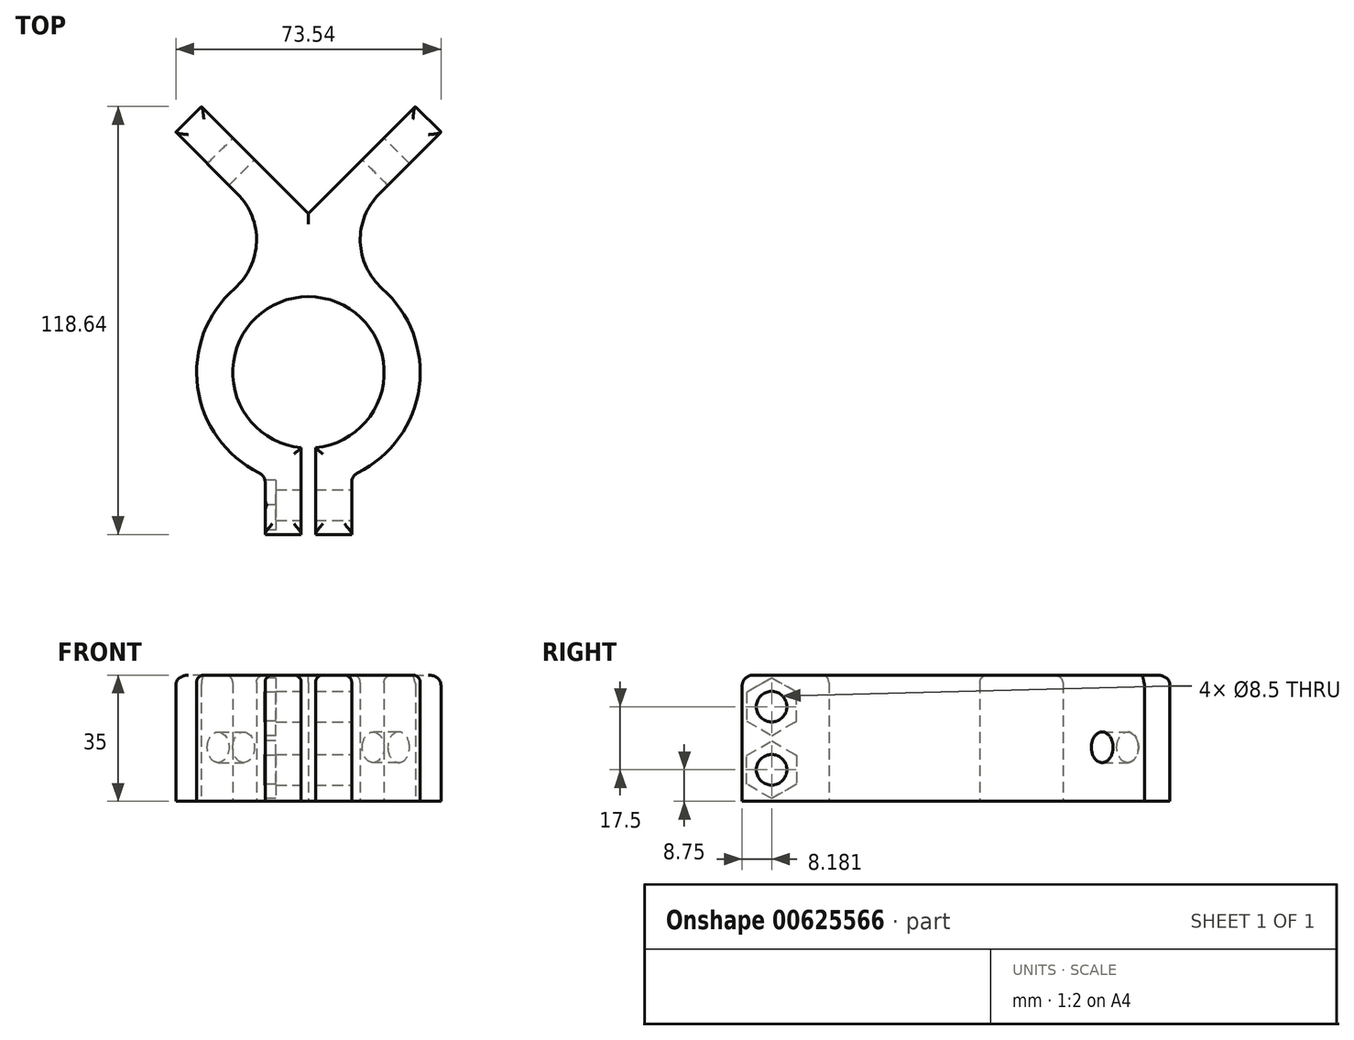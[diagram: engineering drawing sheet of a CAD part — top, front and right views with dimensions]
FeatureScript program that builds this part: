
annotation { "Feature Type Name" : "Feature", "Feature Type Description" : "" }
export const myFeature = defineFeature(function(context is Context, id is Id, definition is map)
    precondition{}
    {
        {
            var Q0;
            Q0=qCreatedBy(makeId("Top.planeOp"),FACE);
            var sketch = newSketch(context, id + "F0", { "sketchPlane" : qUnion([Q0])});
            skLineSegment(sketch, "E0", {"start": v(0, 0) * mm, "end": v(-29.7, 29.7) * mm});
            skLineSegment(sketch, "E1", {"start": v(0, 38.94) * mm, "end": v(0, 0) * mm, "construction": true});
            skLineSegment(sketch, "E2", {"start": v(-29.7, 29.7) * mm, "end": v(-36.77, 22.63) * mm});
            skLineSegment(sketch, "E3", {"start": v(-36.77, 22.63) * mm, "end": v(-1.12, -13.02) * mm});
            skLineSegment(sketch, "E4", {"start": v(0, 0) * mm, "end": v(0, -44) * mm, "construction": true});
            skArc(sketch, "E5", {"start": v(2, -64.9) * mm, "mid": v(0, -23) * mm, "end": v(-2, -64.9) * mm});
            skArc(sketch, "E6", {"start": v(2, -74.94) * mm, "mid": v(31, -43.56) * mm, "end": v(1.12, -13.02) * mm});
            skLineSegment(sketch, "E7", {"start": v(0, -44) * mm, "end": v(0, -75) * mm, "construction": true});
            skLineSegment(sketch, "E8", {"start": v(-2, -74.94) * mm, "end": v(-2, -88.94) * mm});
            skLineSegment(sketch, "E9", {"start": v(-2, -88.94) * mm, "end": v(-12, -88.94) * mm});
            skLineSegment(sketch, "E10", {"start": v(-12, -88.94) * mm, "end": v(-12, -72.58) * mm});
            skLineSegment(sketch, "E11.MirrorCS", {"start": v(2, -88.94) * mm, "end": v(12, -88.94) * mm});
            skLineSegment(sketch, "E12.MirrorCS", {"start": v(12, -88.94) * mm, "end": v(12, -72.58) * mm});
            skLineSegment(sketch, "E13.MirrorCS", {"start": v(2, -74.94) * mm, "end": v(2, -88.94) * mm});
            skLineSegment(sketch, "E14", {"start": v(-2, -74.94) * mm, "end": v(-2, -64.9) * mm});
            skLineSegment(sketch, "E15.MirrorCS", {"start": v(2, -74.94) * mm, "end": v(2, -64.9) * mm});
            skLineSegment(sketch, "E16.MirrorCS", {"start": v(29.7, 29.7) * mm, "end": v(36.77, 22.63) * mm});
            skLineSegment(sketch, "E17.MirrorCS", {"start": v(0, 0) * mm, "end": v(29.7, 29.7) * mm});
            skLineSegment(sketch, "E18.MirrorCS", {"start": v(36.77, 22.63) * mm, "end": v(1.12, -13.02) * mm});
            skPoint(sketch, "E19.orphan", {"position": v(0, -14.14) * mm});
            skArc(sketch, "E20.trimOffspring", {"start": v(-1.12, -13.02) * mm, "mid": v(-31, -43.56) * mm, "end": v(-2, -74.94) * mm});
            skSolve(sketch);
        }
        {
            var Q0;
            Q0=makeQuery(id+"F0.imprint","IMPRINT",FACE,{"disambiguationData":[TD([[makeQuery(id+"F0.imprint","IMPRINT",EDGE,{"derivedFrom":sQuery(id+"F0.wireOp",EDGE,"E0")}),1.0]])]});
            var Q1;
            {var subQ4=sQuery(id+"F0.wireOp",EDGE,"E9");Q1=makeQuery(id+"F0.imprint","IMPRINT",FACE,{"disambiguationData":[TD([[makeQuery(id+"F0.imprint","IMPRINT",EDGE,{"derivedFrom":subQ4}),-1.0]])]});}
            var Q2;
            {var subQ1=sQuery(id+"F0.wireOp",EDGE,"E11.MirrorCS");Q2=makeQuery(id+"F0.imprint","IMPRINT",FACE,{"disambiguationData":[TD([[makeQuery(id+"F0.imprint","IMPRINT",EDGE,{"derivedFrom":subQ1}),1.0]])]});}
            extrude(context, id + "F1", {"entities" : qUnion([Q0, Q1, Q2]), "depth" : 35 * mm, "offsetDistance" : 25 * mm});
        }
        {
            var Q0;
            Q0=makeQuery(id+"F1.opExtrude","SWEPT_FACE",FACE,{"disambiguationData":[OSD([sQuery(id+"F0.wireOp",EDGE,"E17.MirrorCS")])]});
            var sketch = newSketch(context, id + "F2", { "sketchPlane" : qUnion([Q0])});
            skLineSegment(sketch, "E21", {"start": v(0, 15) * mm, "end": v(-50.8, 15) * mm, "construction": true});
            skCircle(sketch, "E22", {"center": v(-25.4, 15) * mm, "radius": 4.25 * mm});
            skSolve(sketch);
        }
        {
            var Q0;
            Q0 = qSketchRegion(id + "F2", true);
            extrude(context, id + "F3", {"entities" : qUnion([Q0]), "operationType" : NewBodyOperationType.REMOVE, "endBound" : BoundingType.UP_TO_NEXT, "oppositeDirection" : true, "depth" : 25 * mm, "offsetDistance" : 25 * mm});
        }
        {
            var Q0;
            Q0=makeQuery(id+"F1.opExtrude","SWEPT_FACE",FACE,{"disambiguationData":[OSD([sQuery(id+"F0.wireOp",EDGE,"E0")])]});
            var sketch = newSketch(context, id + "F4", { "sketchPlane" : qUnion([Q0])});
            skLineSegment(sketch, "E23", {"start": v(0, 15) * mm, "end": v(50.8, 15) * mm, "construction": true});
            skCircle(sketch, "E24", {"center": v(25.4, 15) * mm, "radius": 4.25 * mm});
            skSolve(sketch);
        }
        {
            var Q0;
            Q0 = qSketchRegion(id + "F4", true);
            extrude(context, id + "F5", {"entities" : qUnion([Q0]), "operationType" : NewBodyOperationType.REMOVE, "endBound" : BoundingType.UP_TO_NEXT, "oppositeDirection" : true, "depth" : 25 * mm, "offsetDistance" : 25 * mm});
        }
        {
            var Q0;
            Q0=makeQuery(id+"F1.opExtrude","SWEPT_FACE",FACE,{"disambiguationData":[OSD([sQuery(id+"F0.wireOp",EDGE,"E12.MirrorCS")])]});
            var sketch = newSketch(context, id + "F6", { "sketchPlane" : qUnion([Q0])});
            skLineSegment(sketch, "E25", {"start": v(-80.76, 35) * mm, "end": v(-80.76, 0) * mm, "construction": true});
            skLineSegment(sketch, "E26", {"start": v(-88.94, 17.5) * mm, "end": v(-72.58, 17.5) * mm, "construction": true});
            skLineSegment(sketch, "E27", {"start": v(-88.94, 17.5) * mm, "end": v(-72.58, 35) * mm, "construction": true});
            skCircle(sketch, "E28", {"center": v(-80.76, 26.25) * mm, "radius": 4.25 * mm});
            skCircle(sketch, "E29.MirrorC", {"center": v(-80.76, 8.75) * mm, "radius": 4.25 * mm});
            skLineSegment(sketch, "E30.MirrorCS", {"start": v(-88.94, 17.5) * mm, "end": v(-72.58, 0) * mm, "construction": true});
            skSolve(sketch);
        }
        {
            var Q0;
            Q0 = qSketchRegion(id + "F6", true);
            var Q1;
            Q1=makeQuery(id+"F1.opExtrude","SWEPT_FACE",FACE,{"disambiguationData":[OSD([sQuery(id+"F0.wireOp",EDGE,"E10")])]});
            extrude(context, id + "F7", {"entities" : qUnion([Q0]), "operationType" : NewBodyOperationType.REMOVE, "endBound" : BoundingType.UP_TO_SURFACE, "oppositeDirection" : true, "depth" : 25 * mm, "endBoundEntityFace" : qUnion([Q1]), "offsetDistance" : 25 * mm});
        }
        {
            var Q0;
            Q0=makeQuery(id+"F1.opExtrude","SWEPT_FACE",FACE,{"disambiguationData":[OSD([sQuery(id+"F0.wireOp",EDGE,"E10")])]});
            var sketch = newSketch(context, id + "F8", { "sketchPlane" : qUnion([Q0])});
            skCircle(sketch, "E31.cCircle", {"center": v(80.76, 26.25) * mm, "radius": 6.92 * mm, "construction": true});
            skLineSegment(sketch, "E31.0", {"start": v(80.76, 34.25) * mm, "end": v(87.68, 30.25) * mm});
            skLineSegment(sketch, "E31.1", {"start": v(87.68, 30.25) * mm, "end": v(87.68, 22.25) * mm});
            skLineSegment(sketch, "E31.2", {"start": v(87.68, 22.25) * mm, "end": v(80.76, 18.25) * mm});
            skLineSegment(sketch, "E31.3", {"start": v(80.76, 18.25) * mm, "end": v(73.83, 22.25) * mm});
            skLineSegment(sketch, "E31.4", {"start": v(73.83, 22.25) * mm, "end": v(73.83, 30.25) * mm});
            skLineSegment(sketch, "E31.5", {"start": v(73.83, 30.25) * mm, "end": v(80.76, 34.25) * mm});
            skPoint(sketch, "E31.0.midPoint", {"position": v(84.22, 32.25) * mm});
            skLineSegment(sketch, "E32", {"start": v(88.94, 17.5) * mm, "end": v(74.38, 17.5) * mm, "construction": true});
            skLineSegment(sketch, "E33.MirrorCS", {"start": v(87.68, 12.75) * mm, "end": v(80.76, 16.75) * mm});
            skLineSegment(sketch, "E34.MirrorCS", {"start": v(73.83, 12.75) * mm, "end": v(73.83, 4.75) * mm});
            skLineSegment(sketch, "E35.MirrorCS", {"start": v(80.76, 0.75) * mm, "end": v(87.68, 4.75) * mm});
            skLineSegment(sketch, "E36.MirrorCS", {"start": v(80.76, 16.75) * mm, "end": v(73.83, 12.75) * mm});
            skCircle(sketch, "E37.MirrorC", {"center": v(80.76, 8.75) * mm, "radius": 6.92 * mm, "construction": true});
            skLineSegment(sketch, "E38.MirrorCS", {"start": v(87.68, 4.75) * mm, "end": v(87.68, 12.75) * mm});
            skLineSegment(sketch, "E39.MirrorCS", {"start": v(73.83, 4.75) * mm, "end": v(80.76, 0.75) * mm});
            skPoint(sketch, "E40.MirrorP", {"position": v(84.22, 2.75) * mm});
            skSolve(sketch);
        }
        {
            var Q0;
            Q0 = qSketchRegion(id + "F8", true);
            extrude(context, id + "F9", {"entities" : qUnion([Q0]), "operationType" : NewBodyOperationType.REMOVE, "oppositeDirection" : true, "depth" : 3 * mm, "offsetDistance" : 25 * mm});
        }
        {
            var Q0;
            Q0=makeQuery(id+"F1.opExtrude","SWEPT_EDGE",EDGE,{"disambiguationData":[OSD([sQuery(id+"F0.wireOp",EDGE,"E3"),sQuery(id+"F0.wireOp",EDGE,"E20.trimOffspring")])]});
            var Q1;
            Q1=makeQuery(id+"F1.opExtrude","SWEPT_EDGE",EDGE,{"disambiguationData":[OSD([sQuery(id+"F0.wireOp",EDGE,"E6"),sQuery(id+"F0.wireOp",EDGE,"E18.MirrorCS")])]});
            fillet(context, id + "F10", {"entities" : qUnion([Q0, Q1]), "radius" : 18 * mm, "tangentPropagation" : true, "allowEdgeOverflow" : false});
        }
        {
            var Q0;
            Q0=qCreatedBy(makeId("Right.planeOp"),FACE);
            var sketch = newSketch(context, id + "F11", { "sketchPlane" : qUnion([Q0])});
            skLineSegment(sketch, "E41", {"start": v(-80.12, 22.5) * mm, "end": v(-7.68, 22.5) * mm});
            skLineSegment(sketch, "E42", {"start": v(-7.68, 22.5) * mm, "end": v(-7.68, 58.55) * mm});
            skLineSegment(sketch, "E43", {"start": v(-7.68, 58.55) * mm, "end": v(-80.12, 58.55) * mm});
            skLineSegment(sketch, "E44", {"start": v(-80.12, 58.55) * mm, "end": v(-80.12, 22.5) * mm});
            skSolve(sketch);
        }
        {
            var Q0;
            Q0=makeQuery(id+"F1.opExtrude","CAP_EDGE",EDGE,{"disambiguationData":[OSD([sQuery(id+"F0.wireOp",EDGE,"E9")])],"isStart":false});
            var Q1;
            Q1=makeQuery(id+"F1.opExtrude","CAP_EDGE",EDGE,{"disambiguationData":[OSD([sQuery(id+"F0.wireOp",EDGE,"E11.MirrorCS")])],"isStart":false});
            var Q2;
            Q2=makeQuery(id+"F1.opExtrude","CAP_EDGE",EDGE,{"disambiguationData":[OSD([sQuery(id+"F0.wireOp",EDGE,"E2")])],"isStart":false});
            var Q3;
            Q3=makeQuery(id+"F1.opExtrude","CAP_EDGE",EDGE,{"disambiguationData":[OSD([sQuery(id+"F0.wireOp",EDGE,"E16.MirrorCS")])],"isStart":false});
            var Q4;
            Q4=makeQuery(id+"F1.opExtrude","SWEPT_EDGE",EDGE,{"disambiguationData":[OSD([sQuery(id+"F0.wireOp",EDGE,"E10"),sQuery(id+"F0.wireOp",EDGE,"E20.trimOffspring")])]});
            var Q5;
            Q5=makeQuery(id+"F1.opExtrude","SWEPT_EDGE",EDGE,{"disambiguationData":[OSD([sQuery(id+"F0.wireOp",EDGE,"E6"),sQuery(id+"F0.wireOp",EDGE,"E12.MirrorCS")])]});
            var Q6;
            Q6=makeQuery(id+"FpfucTOSUq623gn_1.boolean.opBoolean","INTERSECT",EDGE,{"derivedFrom":[makeQuery(id+"F1.opExtrude","SWEPT_FACE",FACE,{"disambiguationData":[OSD([sQuery(id+"F0.wireOp",EDGE,"E9")])]}),makeQuery(id+"FpfucTOSUq623gn_1.opExtrude","SWEPT_FACE",FACE,{"disambiguationData":[OSD([sQuery(id+"F11.wireOp",EDGE,"E41")])]})]});
            var Q7;
            Q7=makeQuery(id+"FpfucTOSUq623gn_1.boolean.opBoolean","INTERSECT",EDGE,{"derivedFrom":[makeQuery(id+"F1.opExtrude","SWEPT_FACE",FACE,{"disambiguationData":[OSD([sQuery(id+"F0.wireOp",EDGE,"E11.MirrorCS")])]}),makeQuery(id+"FpfucTOSUq623gn_1.opExtrude","SWEPT_FACE",FACE,{"disambiguationData":[OSD([sQuery(id+"F11.wireOp",EDGE,"E41")])]})]});
            fillet(context, id + "F12", {"entities" : qUnion([Q0, Q1, Q2, Q3, Q4, Q5, Q6, Q7]), "radius" : 3 * mm, "tangentPropagation" : true, "allowEdgeOverflow" : false});
        }
        {
            var Q0;
            Q0=makeQuery(id+"F1.opExtrude","CAP_FACE",FACE,{"disambiguationData":[OSD([sQuery(id+"F0.wireOp",EDGE,"E0"),sQuery(id+"F0.wireOp",EDGE,"E2"),sQuery(id+"F0.wireOp",EDGE,"E3"),sQuery(id+"F0.wireOp",EDGE,"E5"),sQuery(id+"F0.wireOp",EDGE,"E6"),sQuery(id+"F0.wireOp",EDGE,"E8"),sQuery(id+"F0.wireOp",EDGE,"E9"),sQuery(id+"F0.wireOp",EDGE,"E10"),sQuery(id+"F0.wireOp",EDGE,"E11.MirrorCS"),sQuery(id+"F0.wireOp",EDGE,"E12.MirrorCS"),sQuery(id+"F0.wireOp",EDGE,"E13.MirrorCS"),sQuery(id+"F0.wireOp",EDGE,"E14"),sQuery(id+"F0.wireOp",EDGE,"E15.MirrorCS"),sQuery(id+"F0.wireOp",EDGE,"E16.MirrorCS"),sQuery(id+"F0.wireOp",EDGE,"E17.MirrorCS"),sQuery(id+"F0.wireOp",EDGE,"E18.MirrorCS"),sQuery(id+"F0.wireOp",EDGE,"E20.trimOffspring")])],"isStart":false});
            fillet(context, id + "F13", {"entities" : qUnion([Q0]), "radius" : 2 * mm, "allowEdgeOverflow" : false});
        }
    });
